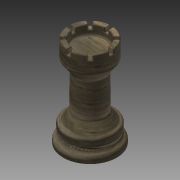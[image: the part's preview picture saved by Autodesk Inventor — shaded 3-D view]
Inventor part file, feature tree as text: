
AUTODESK INVENTOR PART (.ipt)
format: ipt  version: 2015 SP1 (Build 190203100, 203)  size: 555,008 bytes
history: native  units: mm
features: sketch x3, extrude x2, fillet x2, revolve x1
ambient origin geometry x8: Origin, YZ Plane, XZ Plane, XY Plane, X Axis, Y Axis, Z Axis, Center Point
bodies: Solid1 (feature_tree)
feature tree (8):
  revolve  "Revolution1"  [1 undecoded]
  extrude  "Extrusion1"  Depth=1.0mm
  extrude  "Extrusion2"  Depth=0.5mm
  fillet  "Fillet1"  Radius=18.0mm
  fillet  "Fillet2"  Radius=5.0mm
  sketch  "Sketch1"  dims[d10=90.0deg d11=2.0mm]
  sketch  "Sketch2"  dims[d13=1.0mm d14=1.0mm]
  sketch  "Sketch3"  dims[d17=50.0mm d20=2.0mm d21=18.0mm d22=5.0mm d23=0.0mm d24=2.0mm d26=80.0mm d28=360.0deg d30=2.5mm d31=0.0mm d32=1.0mm d33=0.5mm]
note: 1 required parameter value undecoded (feature->parameter linkage not recoverable at this tier; creation-order binding heuristic only, values carry confidence <= 0.55)
